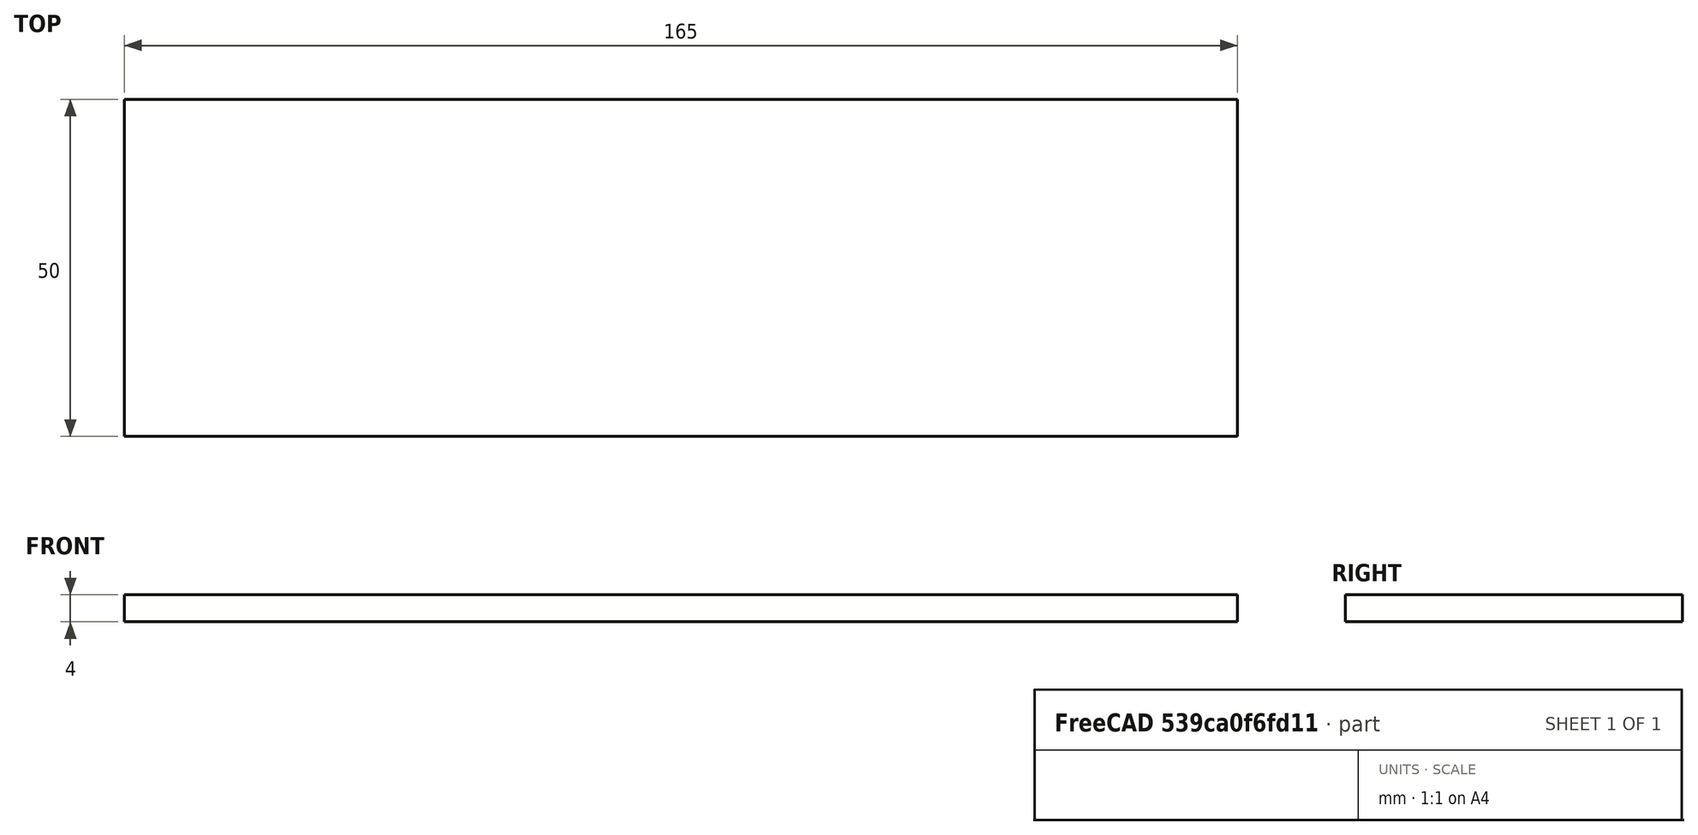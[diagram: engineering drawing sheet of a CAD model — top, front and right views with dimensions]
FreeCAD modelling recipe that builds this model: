
FCSTD DOCUMENT  (FreeCAD 0.17R13528 (Git))
Label: GlassTransparancyShelf
License: All rights reserved
LicenseURL: http://en.wikipedia.org/wiki/All_rights_reserved
objects: Sketcher::SketchObject×1, PartDesign::Pad×1, PartDesign::Body×1
note: 4 computed .brp shape members not serialized (recipe doc carries the construction recipe); baked Part::Feature solids carry a one-line shape summary decoded from their .brp

FEATURE [Sketcher::SketchObject] Sketch
  MapMode = 5
  Support = -> [XY_Plane]
  sketch-geometry (4):
    g0: LineSegment StartX=0 StartY=0 StartZ=0 EndX=165 EndY=0 EndZ=0
    g1: LineSegment StartX=165 StartY=0 StartZ=0 EndX=165 EndY=50 EndZ=0
    g2: LineSegment StartX=165 StartY=50 StartZ=0 EndX=0 EndY=50 EndZ=0
    g3: LineSegment StartX=0 StartY=50 StartZ=0 EndX=0 EndY=0 EndZ=0
  constraints (11):
    c: Coincident(g0,g1)
    c: Coincident(g1,g2)
    c: Coincident(g2,g3)
    c: Coincident(g3,g0)
    c: Horizontal(g0)
    c: Horizontal(g2)
    c: Vertical(g1)
    c: Vertical(g3)
    c: Coincident(g0,g-1)
    c: DistanceY(g1,g1) = 50
    c: DistanceX(g0,g0) = 165
FEATURE [PartDesign::Pad] Pad
  Length = 4
  Length2 = 100
  Profile = -> Sketch
  Reversed = true
  Type = 0
  expr: Length = 4
FEATURE [PartDesign::Body] Body
  Group = -> [Sketch,Pad]
  Origin = -> Origin
  Tip = -> Pad
